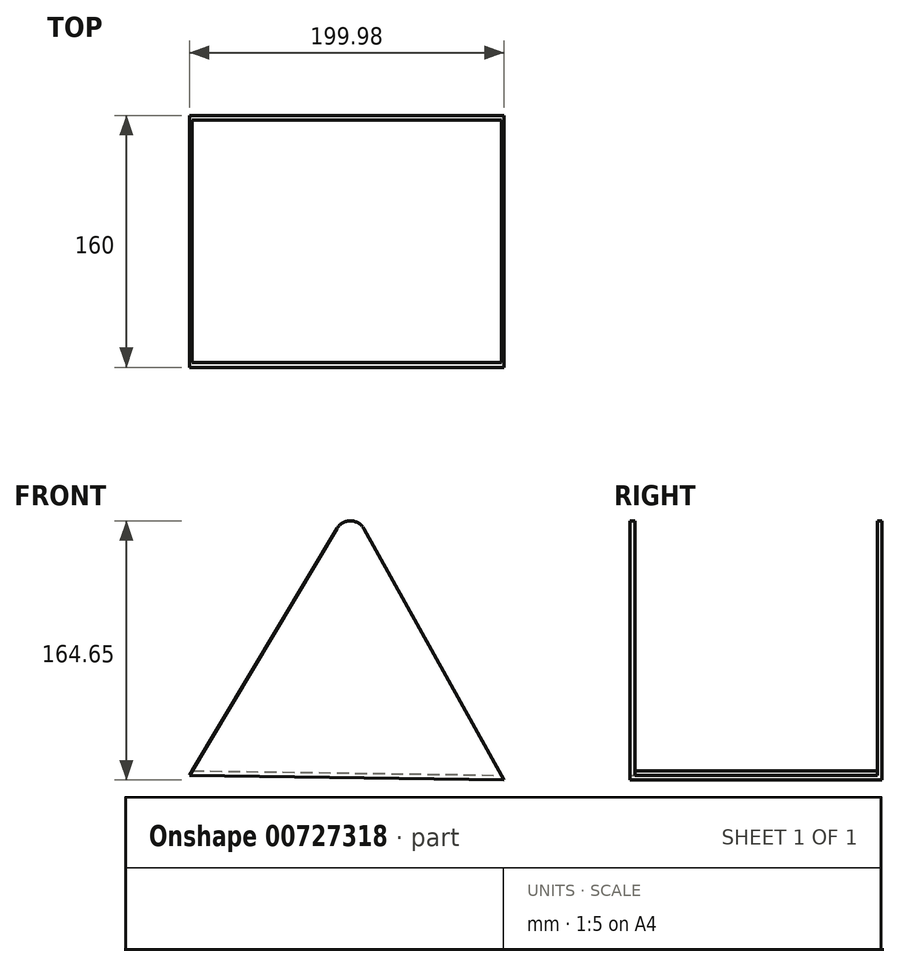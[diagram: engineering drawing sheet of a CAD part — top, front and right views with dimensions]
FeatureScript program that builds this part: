
annotation { "Feature Type Name" : "Feature", "Feature Type Description" : "" }
export const myFeature = defineFeature(function(context is Context, id is Id, definition is map)
    precondition{}
    {
        {
            var Q0;
            Q0=qCreatedBy(makeId("Front.planeOp"),FACE);
            var sketch = newSketch(context, id + "F0", { "sketchPlane" : qUnion([Q0])});
            skLineSegment(sketch, "E0.0", {"start": v(-48.09, 106.76) * mm, "end": v(40.93, -52.76) * mm});
            skLineSegment(sketch, "E0.2", {"start": v(-159.05, -49.84) * mm, "end": v(-65.4, 107.01) * mm});
            skPoint(sketch, "E0.0.midPoint", {"position": v(-27.76, -148.36) * mm});
            skPoint(sketch, "E1.visualSharp", {"position": v(-56.53, 121.88) * mm});
            skArc(sketch, "E1.filletArc", {"start": v(-48.09, 106.76) * mm, "mid": v(-56.68, 111.88) * mm, "end": v(-65.4, 107.01) * mm});
            skLineSegment(sketch, "E2", {"start": v(-159.05, -49.84) * mm, "end": v(40.93, -52.76) * mm});
            skSolve(sketch);
        }
        {
            var Q0;
            Q0=makeQuery(id+"F0.imprint","IMPRINT",FACE,{"disambiguationData":[TD([[makeQuery(id+"F0.imprint","IMPRINT",EDGE,{"derivedFrom":sQuery(id+"F0.wireOp",EDGE,"E0.0")}),-1.0]])]});
            extrude(context, id + "F1", {"entities" : qUnion([Q0]), "depth" : 160 * mm});
        }
        {
            var Q0;
            Q0=makeQuery(id+"F1.opExtrude","SWEPT_FACE",FACE,{"disambiguationData":[OSD([sQuery(id+"F0.wireOp",EDGE,"E2")])]});
            cPlane(context, id + "F2", {"entities" : qUnion([Q0]), "cplaneType" : CPlaneType.OFFSET, "offset" : 3 * mm, "oppositeDirection" : true, "width" : 150 * mm, "height" : 150 * mm});
        }
        {
            var Q0;
            Q0=qCreatedBy(id+"F2.planeOp",FACE);
            var sketch = newSketch(context, id + "F3", { "sketchPlane" : qUnion([Q0])});
            skLineSegment(sketch, "E3.0", {"start": v(-155.3, 3) * mm, "end": v(38.7, 3) * mm});
            skLineSegment(sketch, "E4.1", {"start": v(-155.3, 157) * mm, "end": v(38.7, 157) * mm});
            skLineSegment(sketch, "E5", {"start": v(38.7, 157) * mm, "end": v(52.87, 157) * mm});
            skLineSegment(sketch, "E6", {"start": v(52.87, 157) * mm, "end": v(52.87, 3) * mm});
            skLineSegment(sketch, "E7", {"start": v(52.87, 3) * mm, "end": v(38.7, 3) * mm});
            skLineSegment(sketch, "E8", {"start": v(-155.3, 3) * mm, "end": v(-161.2, 3) * mm});
            skLineSegment(sketch, "E9", {"start": v(-161.2, 3) * mm, "end": v(-161.2, 157) * mm});
            skLineSegment(sketch, "E10", {"start": v(-161.2, 157) * mm, "end": v(-155.3, 157) * mm});
            skSolve(sketch);
        }
        {
            var Q0;
            Q0=qSketchRegion(id+"F3",true);
            extrude(context, id + "F4", {"entities" : qUnion([Q0]), "operationType" : NewBodyOperationType.REMOVE, "oppositeDirection" : true, "depth" : 184 * mm});
        }
    });
